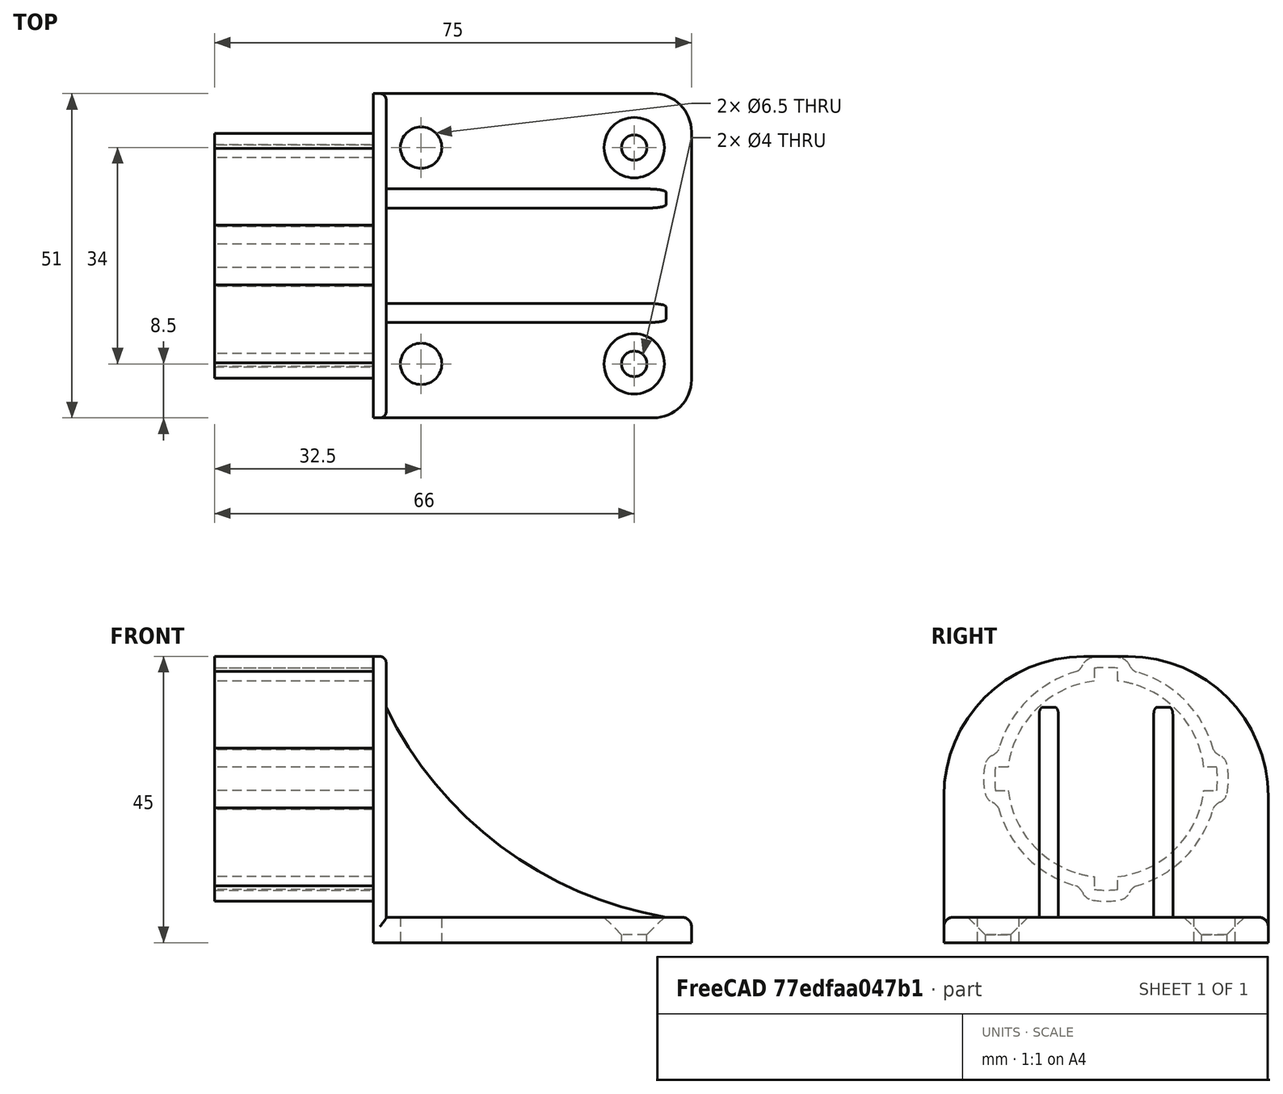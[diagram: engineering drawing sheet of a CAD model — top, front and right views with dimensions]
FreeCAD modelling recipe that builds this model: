
FCSTD DOCUMENT  (FreeCAD 0.20R29410 (Git))
Label: MangoJelly_Solutions_Tutorial_Ep5_2
License: All rights reserved
LicenseURL: http://en.wikipedia.org/wiki/All_rights_reserved
objects: TechDraw::DrawViewDimension×22, App::MeasureDistance×6, PartDesign::Fillet×5, Sketcher::SketchObject×4, PartDesign::Pad×4, Image::ImagePlane×3, TechDraw::DrawProjGroupItem×3, PartDesign::PolarPattern×1, PartDesign::Mirrored×1, PartDesign::Chamfer×1, PartDesign::Body×1, TechDraw::DrawSVGTemplate×1, TechDraw::DrawViewPart×1, TechDraw::DrawViewAnnotation×1, TechDraw::DrawProjGroup×1, TechDraw::DrawPage×1
note: 27 computed .brp shape members not serialized (recipe doc carries the construction recipe); baked Part::Feature solids carry a one-line shape summary decoded from their .brp

FEATURE [Image::ImagePlane] ImagePlane  label="TopPlane"
  Placement = pos=(-24.4487,0.0806853,23) rot=(-0.584068,0.573962,0.573962;4.19884rad)
  XSize = 140.794
  YSize = 93.5123
FEATURE [Image::ImagePlane] ImagePlane001  label="BasePlane"
  Placement = pos=(1,-0.25,2) rot=(0,0,1;0.05236rad)
  XSize = 172.252
  YSize = 114.406
FEATURE [Image::ImagePlane] ImagePlane002  label="SidePlane"
  Placement = pos=(-43.5,-3.3e-15,24) rot=(0,-0.707107,-0.707107;3.14159rad)
  XSize = 169.571
  YSize = 112.626
FEATURE [Sketcher::SketchObject] Sketch001
  FullyConstrained = true
  MapMode = 5
  Support = -> [XY_Plane]
  sketch-geometry (8):
    g0: LineSegment StartX=-24 StartY=25.5 StartZ=0 EndX=24 EndY=25.5 EndZ=0
    g1: LineSegment StartX=24 StartY=25.5 StartZ=0 EndX=24 EndY=-25.5 EndZ=0
    g2: LineSegment StartX=24 StartY=-25.5 StartZ=0 EndX=-24 EndY=-25.5 EndZ=0
    g3: LineSegment StartX=-24 StartY=-25.5 StartZ=0 EndX=-24 EndY=25.5 EndZ=0
    g4: Circle CenterX=-18.5 CenterY=17 CenterZ=0 NormalX=0 NormalY=0 NormalZ=1 AngleXU=0 Radius=3.25
    g5: Circle CenterX=15 CenterY=17 CenterZ=0 NormalX=0 NormalY=0 NormalZ=1 AngleXU=0 Radius=2
    g6: Circle CenterX=-18.5 CenterY=-17 CenterZ=0 NormalX=0 NormalY=0 NormalZ=1 AngleXU=0 Radius=3.25
    g7: Circle CenterX=15 CenterY=-17 CenterZ=0 NormalX=0 NormalY=0 NormalZ=1 AngleXU=0 Radius=2
  constraints (23):
    c: Coincident(g0,g1)
    c: Coincident(g1,g2)
    c: Coincident(g2,g3)
    c: Coincident(g3,g0)
    c: Horizontal(g0)
    c: Horizontal(g2)
    c: Vertical(g1)
    c: Vertical(g3)
    c: DistanceX(g0,g0) = 48
    c: DistanceY(g1,g1) = 51
    c: Symmetric(g0,g2,g-1)
    c: Diameter(g4) = 6.5
    c: Diameter(g5) = 4
    c: Diameter(g6) = 6.5
    c: Diameter(g7) = 4
    c: Horizontal(g7,g6)
    c: Vertical(g6,g4)
    c: Horizontal(g4,g5)
    c: Vertical(g5,g7)
    c: DistanceY(g4,g0) = 8.5
    c: DistanceX(g7,g1) = 9
    c: DistanceX(g0,g4) = 5.5
    c: DistanceY(g1,g7) = 8.5
FEATURE [App::MeasureDistance] Distance  label="Distance: 2.00 mm"
  Distance = 1.99613
  P1 = (-25.8979,-6.23685e-06,19.3175)
  P2 = (-27.8923,-6.22673e-06,19.2326)
FEATURE [App::MeasureDistance] Distance002  label="Distance: 44.63 mm"
  Distance = 44.6289
  P1 = (-26.6385,-3.87683e-06,-0.479858)
  P2 = (-26.955,-9.19687e-06,44.1479)
FEATURE [App::MeasureDistance] Distance003  label="Distance: 25.19 mm"
  Distance = 25.1942
  P1 = (-53.3709,-7.00656e-06,25.7742)
  P2 = (-28.1767,-7.0141e-06,25.8375)
FEATURE [PartDesign::Pad] Pad
  Direction = (0,0,1)
  Length = 4
  Length2 = 10
  Profile = -> Sketch001
  ReferenceAxis = -> Sketch001 [N_Axis]
  Type = 0
FEATURE [Sketcher::SketchObject] Sketch002
  ExternalGeometry = -> [Pad]
  FullyConstrained = true
  MapMode = 5
  Placement = pos=(-24,0,0) rot=(0.57735,-0.57735,-0.57735;2.0944rad)
  Support = -> [Pad]
  sketch-geometry (4):
    g0: LineSegment StartX=-25.5 StartY=0 StartZ=0 EndX=25.5 EndY=0 EndZ=0
    g1: LineSegment StartX=25.5 StartY=0 StartZ=0 EndX=25.5 EndY=45 EndZ=0
    g2: LineSegment StartX=25.5 StartY=45 StartZ=0 EndX=-25.5 EndY=45 EndZ=0
    g3: LineSegment StartX=-25.5 StartY=45 StartZ=0 EndX=-25.5 EndY=0 EndZ=0
  constraints (10):
    c: Coincident(g0,g1)
    c: Coincident(g1,g2)
    c: Coincident(g2,g3)
    c: Coincident(g3,g0)
    c: Horizontal(g2)
    c: Vertical(g1)
    c: Vertical(g3)
    c: Coincident(g0,g-3)
    c: Coincident(g0,g-4)
    c: DistanceY(g1,g1) = 45
FEATURE [PartDesign::Pad] Pad001
  BaseFeature = -> Pad
  Direction = (-1,0,0)
  Length = 2
  Length2 = 10
  Profile = -> Sketch002
  ReferenceAxis = -> Sketch002 [N_Axis]
  Type = 0
FEATURE [Sketcher::SketchObject] Sketch
  AttachmentOffset = pos=(0,25.75,0) rot=(0,0,1;0rad)
  FullyConstrained = true
  MapMode = 5
  Placement = pos=(-26,0,25.75) rot=(0.57735,-0.57735,-0.57735;2.0944rad)
  Support = -> [Pad001]
  sketch-geometry (15):
    g0: LineSegment StartX=0 StartY=0 StartZ=0 EndX=-4.80534 EndY=16.7582 EndZ=0
    g1: LineSegment StartX=0 StartY=0 StartZ=0 EndX=16.8221 EndY=4.82365 EndZ=0
    g2: ArcOfCircle CenterX=0 CenterY=0 CenterZ=0 NormalX=0 NormalY=0 NormalZ=1 AngleXU=0 Radius=17.5 StartAngle=0.279253 EndAngle=1.30693
    g3: ArcOfCircle CenterX=0 CenterY=0 CenterZ=0 NormalX=0 NormalY=0 NormalZ=1 AngleXU=0 Radius=15.5 StartAngle=0.279253 EndAngle=1.45116
    g4: LineSegment StartX=14.8996 StartY=4.27238 StartZ=0 EndX=16.8221 EndY=4.82365 EndZ=0
    g5: LineSegment StartX=-4.27238 StartY=14.8996 StartZ=0 EndX=-4.80534 EndY=16.7582 EndZ=0
    g6: ArcOfCircle CenterX=-5.91183 CenterY=19 CenterZ=0 NormalX=0 NormalY=0 NormalZ=1 AngleXU=0 Radius=2.5 StartAngle=5.17088 EndAngle=5.83823
    g7: ArcOfCircle CenterX=-1.85 CenterY=17.0631 CenterZ=0 NormalX=0 NormalY=0 NormalZ=1 AngleXU=0 Radius=2 StartAngle=1.77215 EndAngle=2.69664
    g8: ArcOfCircle CenterX=9.1e-15 CenterY=8 CenterZ=0 NormalX=0 NormalY=0 NormalZ=1 AngleXU=0 Radius=11.25 StartAngle=1.36944 EndAngle=1.77215
    g9: ArcOfCircle CenterX=1.85 CenterY=17.0631 CenterZ=0 NormalX=0 NormalY=0 NormalZ=1 AngleXU=0 Radius=2 StartAngle=0.444958 EndAngle=1.36944
    g10: ArcOfCircle CenterX=5.91183 CenterY=19 CenterZ=0 NormalX=0 NormalY=0 NormalZ=1 AngleXU=0 Radius=2.5 StartAngle=3.58655 EndAngle=4.14308
    g11: LineSegment StartX=-1.85 StartY=15.3892 StartZ=0 EndX=-1.85 EndY=17.4019 EndZ=0
    g12: LineSegment StartX=1.85 StartY=17.4019 StartZ=0 EndX=1.85 EndY=15.3892 EndZ=0
    g13: ArcOfCircle CenterX=0 CenterY=0 CenterZ=0 NormalX=0 NormalY=0 NormalZ=1 AngleXU=0 Radius=15.5 StartAngle=1.69044 EndAngle=1.85005
    g14: ArcOfCircle CenterX=0 CenterY=0 CenterZ=0 NormalX=0 NormalY=0 NormalZ=1 AngleXU=0 Radius=17.5 StartAngle=1.46488 EndAngle=1.67671
  constraints (43):
    c: Coincident(g0,g-1)
    c: Coincident(g1,g0)
    c: Angle(g1,g0) = 1.5708
    c: Coincident(g2,g0)
    c: Coincident(g2,g1)
    c: Coincident(g3,g2)
    c: PointOnObject(g13,g0)
    c: PointOnObject(g3,g1)
    c: Coincident(g4,g3)
    c: Coincident(g4,g2)
    c: Coincident(g5,g13)
    c: Coincident(g5,g0)
    c: Radius(g2) = 17.5
    c: Radius(g3) = 15.5
    c: Angle(g-1,g1) = 0.279253
    c: Coincident(g6,g0)
    c: Coincident(g8,g7)
    c: Tangent(g7,g6) = 1.5708
    c: Tangent(g10,g9) = 1.5708
    c: DistanceY(g2,g8) = 8
    c: Symmetric(g7,g8,g-2)
    c: Symmetric(g9,g7,g-2)
    c: Symmetric(g10,g6,g-2)
    c: Radius(g6) = 2.5
    c: Radius(g7) = 2
    c: Radius(g8) = 11.25
    c: DistanceX(g7,g9) = 3.7
    c: Coincident(g9,g8)
    c: DistanceX(g7,g8) = 4.5
    c: Vertical(g12)
    c: Vertical(g11)
    c: Symmetric(g11,g12,g-2)
    c: PointOnObject(g7,g11)
    c: Coincident(g14,g11)
    c: DistanceY(g2,g6) = 19
    c: Equal(g3,g13)
    c: PointOnObject(g3,g12)
    c: Coincident(g13,g11)
    c: Coincident(g3,g13)
    c: Equal(g2,g14)
    c: Coincident(g2,g10)
    c: Coincident(g14,g12)
    c: Coincident(g2,g14)
FEATURE [PartDesign::Pad] Pad002
  BaseFeature = -> Pad001
  Direction = (-1,0,0)
  Length = 25
  Length2 = 10
  Profile = -> Sketch
  ReferenceAxis = -> Sketch [N_Axis]
  Type = 0
FEATURE [PartDesign::PolarPattern] PolarPattern
  Angle = 360
  Axis = -> Sketch [N_Axis]
  BaseFeature = -> Pad002
  Occurrences = 4
  Originals = -> [Pad002]
FEATURE [Sketcher::SketchObject] Sketch003
  AttachmentOffset = pos=(0,0,-18) rot=(0,0,1;0rad)
  ExternalGeometry = -> [PolarPattern]
  FullyConstrained = true
  MapMode = 5
  Placement = pos=(0,7.5,4e-15) rot=(0,0.707107,0.707107;3.14159rad)
  Support = -> [PolarPattern]
  sketch-geometry (3):
    g0: ArcOfCircle CenterX=-29.9961 CenterY=63.1615 CenterZ=0 NormalX=0 NormalY=0 NormalZ=1 AngleXU=0 Radius=60 StartAngle=4.87977 EndAngle=5.83201
    g1: LineSegment StartX=24 StartY=37 StartZ=0 EndX=24 EndY=4 EndZ=0
    g2: LineSegment StartX=24 StartY=4 StartZ=0 EndX=-20 EndY=4 EndZ=0
  constraints (9):
    c: PointOnObject(g0,g-3)
    c: PointOnObject(g0,g-4)
    c: Coincident(g0,g1)
    c: Coincident(g1,g2)
    c: Coincident(g2,g0)
    c: DistanceX(g2,g2) = 44
    c: DistanceY(g1,g1) = 33
    c: Radius(g0) = 60
    c: Coincident(g1,g-4)
FEATURE [App::MeasureDistance] Distance004  label="Distance: 3.58 mm"
  Distance = 3.57823
  P1 = (19.8175,9.70815,4)
  P2 = (23.3861,9.44575,4)
FEATURE [PartDesign::Pad] Pad003
  BaseFeature = -> PolarPattern
  Direction = (0,1,-2e-16)
  Length = 3
  Length2 = 10
  Profile = -> Sketch003
  ReferenceAxis = -> Sketch003 [N_Axis]
  Type = 0
FEATURE [PartDesign::Mirrored] Mirrored
  BaseFeature = -> Pad003
  MirrorPlane = -> XZ_Plane
  Originals = -> [Pad003]
FEATURE [App::MeasureDistance] Distance005  label="Distance: 2.90 mm"
  Distance = 2.90213
  P1 = (15.3233,11.8393,4)
  P2 = (15.0217,14.7257,4)
FEATURE [PartDesign::Chamfer] Chamfer
  Angle = 45
  Base = -> Mirrored [Edge31,Edge29]
  BaseFeature = -> Mirrored
  ChamferType = 0
  FlipDirection = false
  Size = 2.75
  Size2 = 1
  SupportTransform = false
  UseAllEdges = false
FEATURE [PartDesign::Fillet] Fillet
  Base = -> Chamfer [Edge22,Edge20]
  BaseFeature = -> Chamfer
  Radius = 6
  SupportTransform = false
  UseAllEdges = false
FEATURE [PartDesign::Fillet] Fillet001
  Base = -> Fillet [Edge58,Edge54]
  BaseFeature = -> Fillet
  Radius = 22
  SupportTransform = false
  UseAllEdges = false
FEATURE [App::MeasureDistance] Distance006  label="Distance: 1.49 mm"
  Distance = 1.49202
  P1 = (11.1179,25.5,4)
  P2 = (11.0267,25.5,2.51077)
FEATURE [PartDesign::Fillet] Fillet002
  Base = -> Fillet001 [Edge23]
  BaseFeature = -> Fillet001
  Radius = 1.5
  SupportTransform = false
  UseAllEdges = false
FEATURE [PartDesign::Fillet] Fillet003
  Base = -> Fillet002 [Edge53,Edge50,Edge40,Edge36]
  BaseFeature = -> Fillet002
  Radius = 0.5
  SupportTransform = false
  UseAllEdges = false
FEATURE [PartDesign::Fillet] Fillet004
  Base = -> Fillet003 [Edge17]
  BaseFeature = -> Fillet003
  Radius = 1
  SupportTransform = false
  UseAllEdges = false
FEATURE [PartDesign::Body] Body
  Group = -> [Sketch,Sketch001,Pad,Sketch002,Pad001,Pad002,PolarPattern,Sketch003,Pad003,Mirrored,Chamfer,Fillet,Fillet001,Fillet002,Fillet003,Fillet004]
  Origin = -> Origin
  Tip = -> Fillet004
FEATURE [TechDraw::DrawSVGTemplate] Template
  Height = 297
  Orientation = 0
  Width = 210
FEATURE [TechDraw::DrawViewPart] View
  Caption = 3D View
  CoarseView = false
  Direction = (0.471,-0.623,0.624)
  Focus = 100
  HardHidden = false
  IsoCount = 0
  IsoHidden = false
  IsoVisible = false
  LockPosition = false
  Perspective = false
  Rotation = 0
  ScaleType = 0
  SeamHidden = false
  SeamVisible = true
  SmoothHidden = false
  SmoothVisible = true
  Source = -> [Body]
  X = 60.2102
  XDirection = (0.79,0.612,0.015)
  Y = 238.592
FEATURE [TechDraw::DrawViewAnnotation] Annotation
  Font = osifont
  LineSpace = 80
  LockPosition = false
  MaxWidth = -1
  Rotation = 0
  ScaleType = 0
  Text = Jai's Strange Object
  TextSize = 12
  TextStyle = 0
  X = 142.665
  Y = 254.226
FEATURE [TechDraw::DrawProjGroupItem] ProjItem  label="Front"
  Caption = Front View
  CoarseView = false
  Direction = (-1,-5e-16,0)
  Focus = 100
  HardHidden = false
  IsoCount = 0
  IsoHidden = false
  IsoVisible = false
  LockPosition = true
  Perspective = false
  Rotation = 0
  RotationVector = (0,-1,0)
  ScaleType = 2
  SeamHidden = false
  SeamVisible = true
  SmoothHidden = false
  SmoothVisible = true
  Source = -> [Body]
  Type = 0
  X = 0
  XDirection = (5e-16,-1,-1e-16)
  Y = 0
FEATURE [TechDraw::DrawProjGroupItem] ProjItem001  label="Right"
  Caption = Side View
  CoarseView = false
  Direction = (4e-16,-1,-1e-16)
  Focus = 100
  HardHidden = false
  IsoCount = 0
  IsoHidden = false
  IsoVisible = false
  LockPosition = false
  Perspective = false
  Rotation = 0
  RotationVector = (1,0,0)
  ScaleType = 2
  SeamHidden = false
  SeamVisible = true
  SmoothHidden = false
  SmoothVisible = true
  Source = -> [Body]
  Type = 2
  X = -87.0395
  XDirection = (1,4e-16,0)
  Y = 0
FEATURE [TechDraw::DrawProjGroupItem] ProjItem002  label="Top"
  Caption = Top View
  CoarseView = false
  Direction = (0,-1e-16,1)
  Focus = 100
  HardHidden = false
  IsoCount = 0
  IsoHidden = false
  IsoVisible = false
  LockPosition = false
  Perspective = false
  Rotation = 0
  RotationVector = (1,0,0)
  ScaleType = 2
  SeamHidden = false
  SeamVisible = true
  SmoothHidden = false
  SmoothVisible = true
  Source = -> [Body]
  Type = 4
  X = 0
  XDirection = (5e-16,-1,-1e-16)
  Y = 93.1082
FEATURE [TechDraw::DrawProjGroup] ProjGroup
  Anchor = -> ProjItem
  AutoDistribute = false
  LockPosition = false
  ProjectionType = 0
  Rotation = 0
  ScaleType = 0
  Source = -> [Body]
  Views = -> [ProjItem,ProjItem001,ProjItem002]
  X = 149.839
  Y = 57.4787
  spacingX = 15
  spacingY = 15
FEATURE [TechDraw::DrawViewDimension] Dimension002
  AngleOverride = false
  Arbitrary = false
  ArbitraryTolerances = false
  EqualTolerance = true
  ExtensionAngle = 0
  FormatSpec = R%.2w
  FormatSpecOverTolerance = %+.2w
  FormatSpecUnderTolerance = %+.2w
  Inverted = false
  LineAngle = 0
  LockPosition = false
  MeasureType = 1
  OverTolerance = 0
  References2D = -> [ProjItem001]
  Rotation = 0
  ScaleType = 0
  TheoreticalExact = false
  Type = 4
  UnderTolerance = 0
  X = 27.0235
  Y = 26.5491
FEATURE [TechDraw::DrawViewDimension] Dimension003
  AngleOverride = false
  Arbitrary = false
  ArbitraryTolerances = false
  EqualTolerance = true
  ExtensionAngle = 0
  FormatSpec = %.2w
  FormatSpecOverTolerance = %+.2w
  FormatSpecUnderTolerance = %+.2w
  Inverted = false
  LineAngle = 0
  LockPosition = false
  MeasureType = 1
  OverTolerance = 0
  References2D = -> [ProjItem001]
  Rotation = 0
  ScaleType = 0
  TheoreticalExact = false
  Type = 1
  UnderTolerance = 0
  X = -25.3479
  Y = 36.5298
FEATURE [TechDraw::DrawViewDimension] Dimension004
  AngleOverride = false
  Arbitrary = false
  ArbitraryTolerances = false
  EqualTolerance = true
  ExtensionAngle = 0
  FormatSpec = %.2w
  FormatSpecOverTolerance = %+.2w
  FormatSpecUnderTolerance = %+.2w
  Inverted = false
  LineAngle = 0
  LockPosition = false
  MeasureType = 1
  OverTolerance = 0
  References2D = -> [ProjItem001]
  Rotation = 0
  ScaleType = 0
  TheoreticalExact = false
  Type = 1
  UnderTolerance = 0
  X = 0.426206
  Y = 30.23
FEATURE [TechDraw::DrawViewDimension] Dimension005
  AngleOverride = false
  Arbitrary = false
  ArbitraryTolerances = false
  EqualTolerance = true
  ExtensionAngle = 0
  FormatSpec = %.2w
  FormatSpecOverTolerance = %+.2w
  FormatSpecUnderTolerance = %+.2w
  Inverted = false
  LineAngle = 0
  LockPosition = false
  MeasureType = 1
  OverTolerance = 0
  References2D = -> [ProjItem001]
  Rotation = 0
  ScaleType = 0
  TheoreticalExact = false
  Type = 2
  UnderTolerance = 0
  X = 43.3949
  Y = -32.7622
FEATURE [TechDraw::DrawViewDimension] Dimension006
  AngleOverride = false
  Arbitrary = false
  ArbitraryTolerances = false
  EqualTolerance = true
  ExtensionAngle = 0
  FormatSpec = %.2w
  FormatSpecOverTolerance = %+.2w
  FormatSpecUnderTolerance = %+.2w
  Inverted = false
  LineAngle = 0
  LockPosition = false
  MeasureType = 1
  OverTolerance = 0
  References2D = -> [ProjItem001]
  Rotation = 0
  ScaleType = 0
  TheoreticalExact = false
  Type = 1
  UnderTolerance = 0
  X = 12.2
  Y = -34.23
FEATURE [TechDraw::DrawViewDimension] Dimension007
  AngleOverride = false
  Arbitrary = false
  ArbitraryTolerances = false
  EqualTolerance = true
  ExtensionAngle = 0
  FormatSpec = %.2w
  FormatSpecOverTolerance = %+.2w
  FormatSpecUnderTolerance = %+.2w
  Inverted = false
  LineAngle = 0
  LockPosition = false
  MeasureType = 1
  OverTolerance = 0
  References2D = -> [ProjItem001]
  Rotation = 0
  ScaleType = 0
  TheoreticalExact = false
  Type = 2
  UnderTolerance = 0
  X = 30.3548
  Y = -0.802596
FEATURE [TechDraw::DrawViewDimension] Dimension008
  AngleOverride = false
  Arbitrary = false
  ArbitraryTolerances = false
  EqualTolerance = true
  ExtensionAngle = 0
  FormatSpec = %.2w
  FormatSpecOverTolerance = %+.2w
  FormatSpecUnderTolerance = %+.2w
  Inverted = false
  LineAngle = 0
  LockPosition = false
  MeasureType = 1
  OverTolerance = 0
  References2D = -> [ProjItem001]
  Rotation = 0
  ScaleType = 0
  TheoreticalExact = false
  Type = 2
  UnderTolerance = 0
  X = -44.3721
  Y = 5.38592
FEATURE [TechDraw::DrawViewDimension] Dimension009
  AngleOverride = false
  Arbitrary = false
  ArbitraryTolerances = false
  EqualTolerance = true
  ExtensionAngle = 0
  FormatSpec = %.2w
  FormatSpecOverTolerance = %+.2w
  FormatSpecUnderTolerance = %+.2w
  Inverted = false
  LineAngle = 0
  LockPosition = false
  MeasureType = 1
  OverTolerance = 0
  References2D = -> [ProjItem001]
  Rotation = 0
  ScaleType = 0
  TheoreticalExact = false
  Type = 2
  UnderTolerance = 0
  X = -55.2448
  Y = -19.7898
FEATURE [TechDraw::DrawViewDimension] Dimension
  AngleOverride = false
  Arbitrary = false
  ArbitraryTolerances = false
  EqualTolerance = true
  ExtensionAngle = 0
  FormatSpec = ⌀%.2w
  FormatSpecOverTolerance = %+.2w
  FormatSpecUnderTolerance = %+.2w
  Inverted = false
  LineAngle = 0
  LockPosition = false
  MeasureType = 1
  OverTolerance = 0
  References2D = -> [ProjItem]
  Rotation = 0
  ScaleType = 0
  TheoreticalExact = false
  Type = 5
  UnderTolerance = 0
  X = 22.2096
  Y = 36.1128
FEATURE [TechDraw::DrawViewDimension] Dimension010
  AngleOverride = false
  Arbitrary = false
  ArbitraryTolerances = false
  EqualTolerance = true
  ExtensionAngle = 0
  FormatSpec = ⌀%.2w
  FormatSpecOverTolerance = %+.2w
  FormatSpecUnderTolerance = %+.2w
  Inverted = false
  LineAngle = 0
  LockPosition = false
  MeasureType = 1
  OverTolerance = 0
  References2D = -> [ProjItem]
  Rotation = 0
  ScaleType = 0
  TheoreticalExact = false
  Type = 5
  UnderTolerance = 0
  X = 31.0002
  Y = 29.6921
FEATURE [TechDraw::DrawViewDimension] Dimension011
  AngleOverride = false
  Arbitrary = false
  ArbitraryTolerances = false
  EqualTolerance = true
  ExtensionAngle = 0
  FormatSpec = %.2w
  FormatSpecOverTolerance = %+.2w
  FormatSpecUnderTolerance = %+.2w
  Inverted = false
  LineAngle = 0
  LockPosition = false
  MeasureType = 1
  OverTolerance = 0
  References2D = -> [ProjItem]
  Rotation = 0
  ScaleType = 0
  TheoreticalExact = false
  Type = 2
  UnderTolerance = 0
  X = 31.8696
  Y = -22.3845
FEATURE [TechDraw::DrawViewDimension] Dimension012
  AngleOverride = false
  Arbitrary = false
  ArbitraryTolerances = false
  EqualTolerance = true
  ExtensionAngle = 0
  FormatSpec = %.2w
  FormatSpecOverTolerance = %+.2w
  FormatSpecUnderTolerance = %+.2w
  Inverted = false
  LineAngle = 0
  LockPosition = false
  MeasureType = 1
  OverTolerance = 0
  References2D = -> [ProjItem]
  Rotation = 0
  ScaleType = 0
  TheoreticalExact = false
  Type = 2
  UnderTolerance = 0
  X = 37.1475
  Y = 16.0777
FEATURE [TechDraw::DrawViewDimension] Dimension013
  AngleOverride = false
  Arbitrary = false
  ArbitraryTolerances = false
  EqualTolerance = true
  ExtensionAngle = 0
  FormatSpec = ⌀%.2w
  FormatSpecOverTolerance = %+.2w
  FormatSpecUnderTolerance = %+.2w
  Inverted = false
  LineAngle = 0
  LockPosition = false
  MeasureType = 1
  OverTolerance = 0
  References2D = -> [ProjItem002]
  Rotation = 0
  ScaleType = 0
  TheoreticalExact = false
  Type = 5
  UnderTolerance = 0
  X = -7.53668
  Y = 47.4315
FEATURE [TechDraw::DrawViewDimension] Dimension014
  AngleOverride = false
  Arbitrary = false
  ArbitraryTolerances = false
  EqualTolerance = true
  ExtensionAngle = 0
  FormatSpec = %.2w
  FormatSpecOverTolerance = %+.2w
  FormatSpecUnderTolerance = %+.2w
  Inverted = false
  LineAngle = 0
  LockPosition = false
  MeasureType = 1
  OverTolerance = 0
  References2D = -> [ProjItem002]
  Rotation = 0
  ScaleType = 0
  TheoreticalExact = false
  Type = 2
  UnderTolerance = 0
  X = -37.1741
  Y = 23.3469
FEATURE [TechDraw::DrawViewDimension] Dimension015
  AngleOverride = false
  Arbitrary = false
  ArbitraryTolerances = false
  EqualTolerance = true
  ExtensionAngle = 0
  FormatSpec = %.2w
  FormatSpecOverTolerance = %+.2w
  FormatSpecUnderTolerance = %+.2w
  Inverted = false
  LineAngle = 0
  LockPosition = false
  MeasureType = 1
  OverTolerance = 0
  References2D = -> [ProjItem002]
  Rotation = 0
  ScaleType = 0
  TheoreticalExact = false
  Type = 1
  UnderTolerance = 0
  X = 17.3922
  Y = 46.4626
FEATURE [TechDraw::DrawViewDimension] Dimension016
  AngleOverride = false
  Arbitrary = false
  ArbitraryTolerances = false
  EqualTolerance = true
  ExtensionAngle = 0
  FormatSpec = %.2w
  FormatSpecOverTolerance = %+.2w
  FormatSpecUnderTolerance = %+.2w
  Inverted = false
  LineAngle = 0
  LockPosition = false
  MeasureType = 1
  OverTolerance = 0
  References2D = -> [ProjItem002]
  Rotation = 0
  ScaleType = 0
  TheoreticalExact = false
  Type = 1
  UnderTolerance = 0
  X = 17.1439
  Y = 58.7739
FEATURE [TechDraw::DrawViewDimension] Dimension017
  AngleOverride = false
  Arbitrary = false
  ArbitraryTolerances = false
  EqualTolerance = true
  ExtensionAngle = 0
  FormatSpec = ⌀%.2w
  FormatSpecOverTolerance = %+.2w
  FormatSpecUnderTolerance = %+.2w
  Inverted = false
  LineAngle = 0
  LockPosition = false
  MeasureType = 1
  OverTolerance = 0
  References2D = -> [ProjItem]
  Rotation = 0
  ScaleType = 0
  TheoreticalExact = false
  Type = 5
  UnderTolerance = 0
  X = -26.8627
  Y = 29.1722
FEATURE [TechDraw::DrawViewDimension] Dimension018
  AngleOverride = false
  Arbitrary = false
  ArbitraryTolerances = false
  EqualTolerance = true
  ExtensionAngle = 0
  FormatSpec = %.2w
  FormatSpecOverTolerance = %+.2w
  FormatSpecUnderTolerance = %+.2w
  Inverted = false
  LineAngle = 0
  LockPosition = false
  MeasureType = 1
  OverTolerance = 0
  References2D = -> [ProjItem002]
  Rotation = 0
  ScaleType = 0
  TheoreticalExact = false
  Type = 2
  UnderTolerance = 0
  X = 31.7653
  Y = 46.6255
FEATURE [TechDraw::DrawViewDimension] Dimension019
  AngleOverride = false
  Arbitrary = false
  ArbitraryTolerances = false
  EqualTolerance = true
  ExtensionAngle = 0
  FormatSpec = %.2w
  FormatSpecOverTolerance = %+.2w
  FormatSpecUnderTolerance = %+.2w
  Inverted = false
  LineAngle = 0
  LockPosition = false
  MeasureType = 1
  OverTolerance = 0
  References2D = -> [ProjItem002]
  Rotation = 0
  ScaleType = 0
  TheoreticalExact = false
  Type = 1
  UnderTolerance = 0
  X = 48.0503
  Y = 24.0886
FEATURE [TechDraw::DrawViewDimension] Dimension020
  AngleOverride = false
  Arbitrary = false
  ArbitraryTolerances = false
  EqualTolerance = true
  ExtensionAngle = 0
  FormatSpec = %.2w
  FormatSpecOverTolerance = %+.2w
  FormatSpecUnderTolerance = %+.2w
  Inverted = false
  LineAngle = 0
  LockPosition = false
  MeasureType = 1
  OverTolerance = 0
  References2D = -> [ProjItem002]
  Rotation = 0
  ScaleType = 0
  TheoreticalExact = false
  Type = 1
  UnderTolerance = 0
  X = 34.6379
  Y = -14.8749
FEATURE [TechDraw::DrawViewDimension] Dimension021
  AngleOverride = false
  Arbitrary = false
  ArbitraryTolerances = false
  EqualTolerance = true
  ExtensionAngle = 0
  FormatSpec = %.2w
  FormatSpecOverTolerance = %+.2w
  FormatSpecUnderTolerance = %+.2w
  Inverted = false
  LineAngle = 0
  LockPosition = false
  MeasureType = 1
  OverTolerance = 0
  References2D = -> [ProjItem002]
  Rotation = 0
  ScaleType = 0
  TheoreticalExact = false
  Type = 2
  UnderTolerance = 0
  X = 42.4344
  Y = 5.28136
FEATURE [TechDraw::DrawViewDimension] Dimension022
  AngleOverride = false
  Arbitrary = false
  ArbitraryTolerances = false
  EqualTolerance = true
  ExtensionAngle = 0
  FormatSpec = ⌀%.2w
  FormatSpecOverTolerance = %+.2w
  FormatSpecUnderTolerance = %+.2w
  Inverted = false
  LineAngle = 0
  LockPosition = false
  MeasureType = 1
  OverTolerance = 0
  References2D = -> [ProjItem002]
  Rotation = 0
  ScaleType = 0
  TheoreticalExact = false
  Type = 5
  UnderTolerance = 0
  X = -37.6821
  Y = 3.32881
FEATURE [TechDraw::DrawPage] Page
  KeepUpdated = true
  NextBalloonIndex = 1
  ProjectionType = 0
  Template = -> Template
  Views = -> [View,Annotation,ProjGroup,Dimension002,Dimension003,Dimension004,Dimension005,Dimension006,Dimension007,Dimension008,Dimension009,Dimension,Dimension010,Dimension011,Dimension012,Dimension013,Dimension014,Dimension015,Dimension016,Dimension017,Dimension018,Dimension019,Dimension020,Dimension021,Dimension022]
